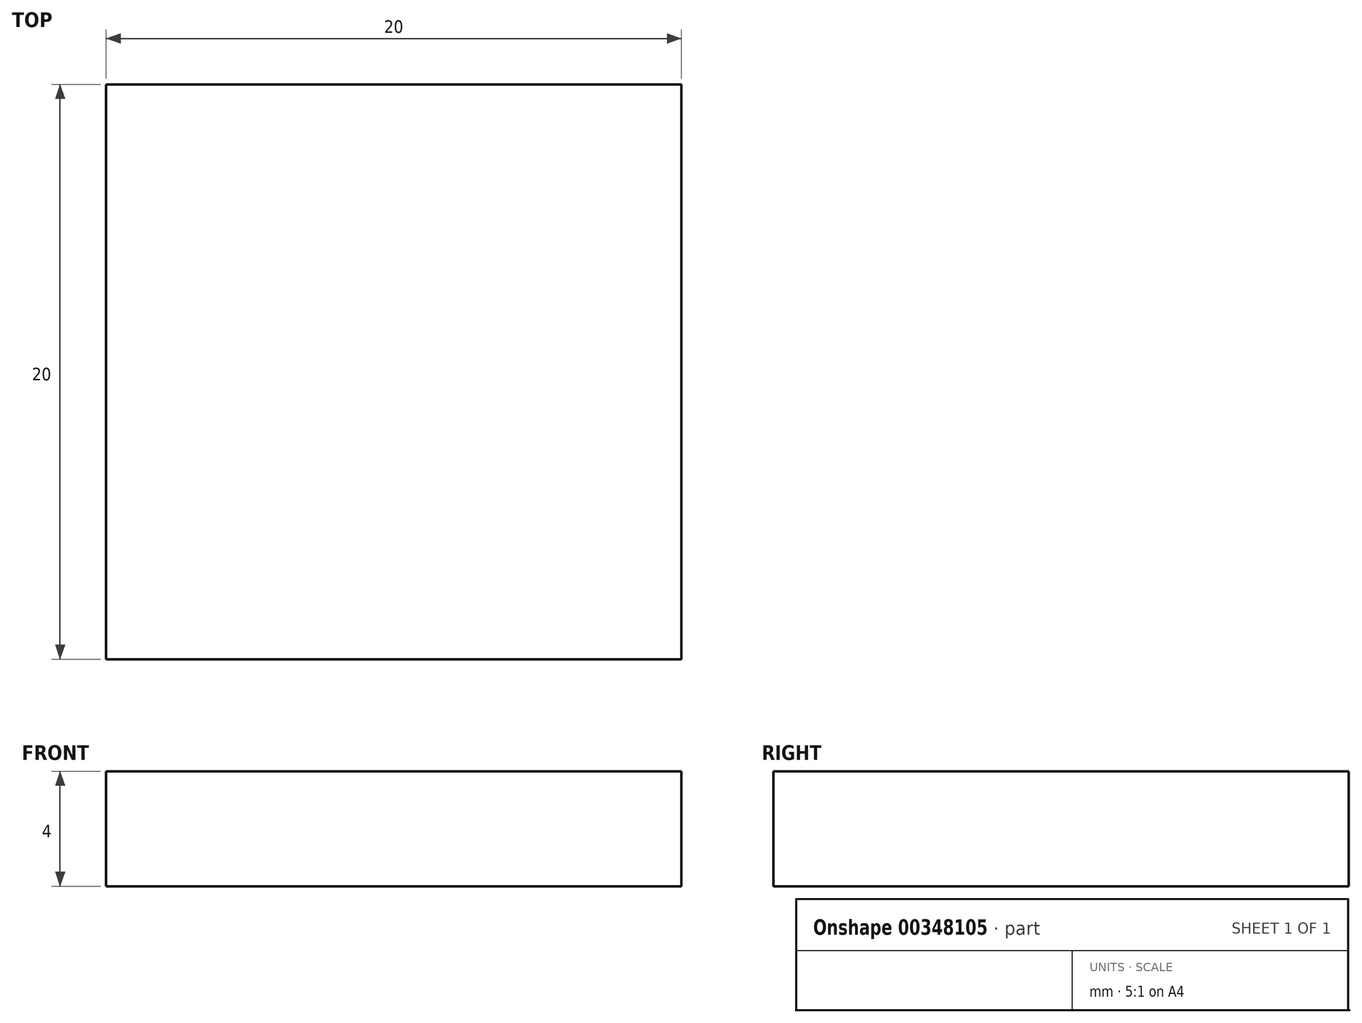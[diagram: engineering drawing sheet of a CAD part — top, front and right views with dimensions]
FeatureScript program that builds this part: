
annotation { "Feature Type Name" : "Feature", "Feature Type Description" : "" }
export const myFeature = defineFeature(function(context is Context, id is Id, definition is map)
    precondition{}
    {
        {
            var Q0;
            Q0=qCreatedBy(makeId("Top.planeOp"),FACE);
            var sketch = newSketch(context, id + "F0", { "sketchPlane" : qUnion([Q0])});
            skLineSegment(sketch, "E0.bottom", {"start": v(0, 0) * mm, "end": v(20, 0) * mm});
            skLineSegment(sketch, "E0.top", {"start": v(0, 20) * mm, "end": v(20, 20) * mm});
            skLineSegment(sketch, "E0.left", {"start": v(0, 0) * mm, "end": v(0, 20) * mm});
            skLineSegment(sketch, "E0.right", {"start": v(20, 0) * mm, "end": v(20, 20) * mm});
            skSolve(sketch);
        }
        {
            var Q0;
            Q0=makeQuery(id+"F0.imprint","IMPRINT",FACE,{"disambiguationData":[TD([[makeQuery(id+"F0.imprint","IMPRINT",EDGE,{"derivedFrom":sQuery(id+"F0.wireOp",EDGE,"E0.bottom")}),1.0]])]});
            extrude(context, id + "F1", {"entities" : qUnion([Q0]), "depth" : 4 * mm});
        }
    });
